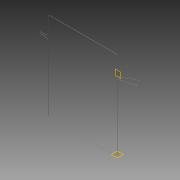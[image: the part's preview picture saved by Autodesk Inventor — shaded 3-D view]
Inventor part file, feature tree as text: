
AUTODESK INVENTOR PART (.ipt)
format: ipt  version: 2013 (Build 170138000, 138)  size: 109,568 bytes
history: native  units: in
note: dims shown in document units (in); Inventor stores cm internally (conversion verified against a paired STEP export)
features: reference x10, plane x2, sketch x2, sweep x1
ambient origin geometry x8: Origin, YZ Plane, XZ Plane, XY Plane, X Axis, Y Axis, Z Axis, Center Point
bodies: Solid1 (feature_tree)
feature tree (15):
  plane  "Work Plane3"
  sketch  "Sketch4"  dims[d5=-0.0984in d6=0.0197in]
  plane  "Work Plane4"
  sweep  "Sweep1"
  reference  "Reference21"
  reference  "Reference22"
  reference  "Reference23"
  reference  "Reference24"
  reference  "Reference25"
  reference  "Reference26"
  reference  "Reference27"
  reference  "Reference28"
  reference  "Reference29"
  reference  "Reference30"
  sketch  "Sketch5"  dims[d7=0.0394in d9=0.0in]
